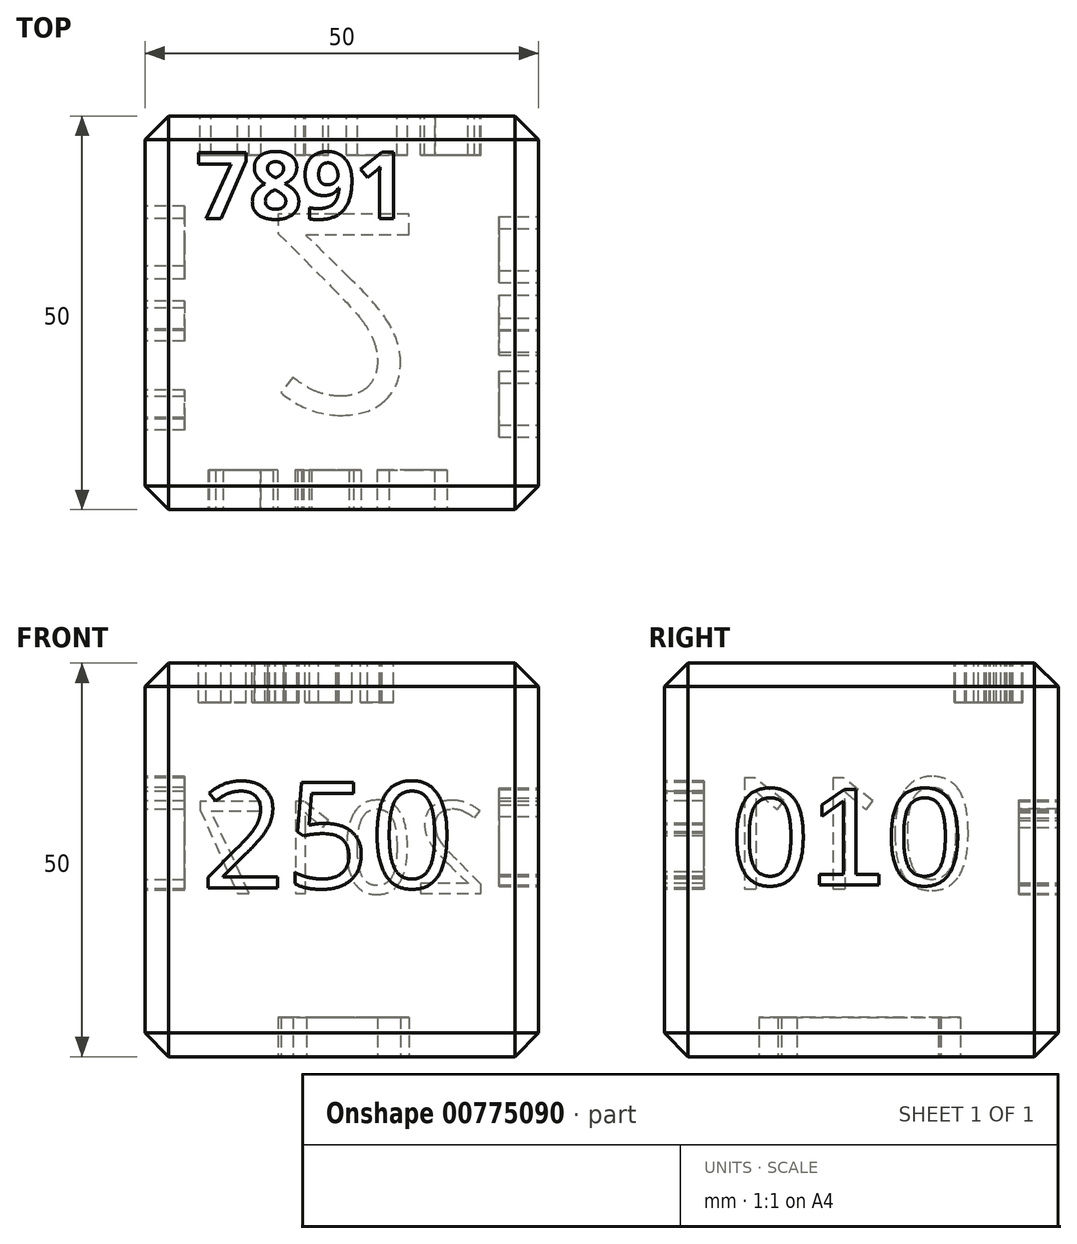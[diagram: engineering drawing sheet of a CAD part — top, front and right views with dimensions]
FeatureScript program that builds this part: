
annotation { "Feature Type Name" : "Feature", "Feature Type Description" : "" }
export const myFeature = defineFeature(function(context is Context, id is Id, definition is map)
    precondition{}
    {
        {
            var Q0;
            Q0=qCreatedBy(makeId("Top.planeOp"),FACE);
            var sketch = newSketch(context, id + "F0", { "sketchPlane" : qUnion([Q0])});
            skLineSegment(sketch, "E0.bottom", {"start": v(-32.37, 24.04) * mm, "end": v(17.63, 24.04) * mm});
            skLineSegment(sketch, "E0.top", {"start": v(-32.37, -25.96) * mm, "end": v(17.63, -25.96) * mm});
            skLineSegment(sketch, "E0.left", {"start": v(-32.37, 24.04) * mm, "end": v(-32.37, -25.96) * mm});
            skLineSegment(sketch, "E0.right", {"start": v(17.63, 24.04) * mm, "end": v(17.63, -25.96) * mm});
            skSolve(sketch);
        }
        {
            var Q0;
            Q0=makeQuery(id+"F0.imprint","IMPRINT",FACE,{"disambiguationData":[TD([[makeQuery(id+"F0.imprint","IMPRINT",EDGE,{"derivedFrom":sQuery(id+"F0.wireOp",EDGE,"E0.bottom")}),-1.0]])]});
            extrude(context, id + "F1", {"entities" : qUnion([Q0]), "depth" : 50 * mm, "offsetDistance" : 25 * mm});
        }
        {
            var Q0;
            Q0=makeQuery(id+"F1.opExtrude","CAP_EDGE",EDGE,{"disambiguationData":[OSD([sQuery(id+"F0.wireOp",EDGE,"E0.right")])],"isStart":false});
            var Q1;
            Q1=makeQuery(id+"F1.opExtrude","CAP_EDGE",EDGE,{"disambiguationData":[OSD([sQuery(id+"F0.wireOp",EDGE,"E0.top")])],"isStart":false});
            var Q2;
            Q2=makeQuery(id+"F1.opExtrude","CAP_EDGE",EDGE,{"disambiguationData":[OSD([sQuery(id+"F0.wireOp",EDGE,"E0.left")])],"isStart":false});
            var Q3;
            Q3=makeQuery(id+"F1.opExtrude","CAP_EDGE",EDGE,{"disambiguationData":[OSD([sQuery(id+"F0.wireOp",EDGE,"E0.bottom")])],"isStart":false});
            var Q4;
            Q4=makeQuery(id+"F1.opExtrude","CAP_EDGE",EDGE,{"disambiguationData":[OSD([sQuery(id+"F0.wireOp",EDGE,"E0.top")])],"isStart":true});
            var Q5;
            Q5=makeQuery(id+"F1.opExtrude","CAP_EDGE",EDGE,{"disambiguationData":[OSD([sQuery(id+"F0.wireOp",EDGE,"E0.left")])],"isStart":true});
            var Q6;
            Q6=makeQuery(id+"F1.opExtrude","CAP_EDGE",EDGE,{"disambiguationData":[OSD([sQuery(id+"F0.wireOp",EDGE,"E0.bottom")])],"isStart":true});
            var Q7;
            Q7=makeQuery(id+"F1.opExtrude","CAP_EDGE",EDGE,{"disambiguationData":[OSD([sQuery(id+"F0.wireOp",EDGE,"E0.right")])],"isStart":true});
            var Q8;
            Q8=makeQuery(id+"F1.opExtrude","SWEPT_EDGE",EDGE,{"disambiguationData":[OSD([sQuery(id+"F0.wireOp",EDGE,"E0.bottom"),sQuery(id+"F0.wireOp",EDGE,"E0.right")])]});
            var Q9;
            Q9=makeQuery(id+"F1.opExtrude","SWEPT_EDGE",EDGE,{"disambiguationData":[OSD([sQuery(id+"F0.wireOp",EDGE,"E0.bottom"),sQuery(id+"F0.wireOp",EDGE,"E0.left")])]});
            var Q10;
            Q10=makeQuery(id+"F1.opExtrude","SWEPT_EDGE",EDGE,{"disambiguationData":[OSD([sQuery(id+"F0.wireOp",EDGE,"E0.top"),sQuery(id+"F0.wireOp",EDGE,"E0.left")])]});
            var Q11;
            Q11=makeQuery(id+"F1.opExtrude","SWEPT_EDGE",EDGE,{"disambiguationData":[OSD([sQuery(id+"F0.wireOp",EDGE,"E0.top"),sQuery(id+"F0.wireOp",EDGE,"E0.right")])]});
            chamfer(context, id + "F2", {"entities" : qUnion([Q0, Q1, Q2, Q3, Q4, Q5, Q6, Q7, Q8, Q9, Q10, Q11]), "width" : 3 * mm, "tangentPropagation" : true});
        }
        {
            var Q0;
            Q0=makeQuery(id+"F1.opExtrude","CAP_FACE",FACE,{"disambiguationData":[OSD([sQuery(id+"F0.wireOp",EDGE,"E0.bottom"),sQuery(id+"F0.wireOp",EDGE,"E0.top"),sQuery(id+"F0.wireOp",EDGE,"E0.left"),sQuery(id+"F0.wireOp",EDGE,"E0.right")])],"isStart":false});
            var sketch = newSketch(context, id + "F3", { "sketchPlane" : qUnion([Q0])});
            skText(sketch, "E1", { "text": "7891\n", "fontName": "OpenSans-Bold.ttf"});
            const initialGuessF3  = {"E1": [-0.02589, 0.011, 1, 0, 0.0085]};
            skSetInitialGuess(sketch, initialGuessF3);
            skSolve(sketch);
        }
        {
            var Q0;
            Q0 = qSketchRegion(id + "F3", true);
            extrude(context, id + "F4", {"entities" : qUnion([Q0]), "operationType" : NewBodyOperationType.REMOVE, "oppositeDirection" : true, "depth" : 5 * mm, "offsetDistance" : 25 * mm});
        }
        {
            var Q0;
            Q0=makeQuery(id+"F1.opExtrude","CAP_FACE",FACE,{"disambiguationData":[OSD([sQuery(id+"F0.wireOp",EDGE,"E0.bottom"),sQuery(id+"F0.wireOp",EDGE,"E0.top"),sQuery(id+"F0.wireOp",EDGE,"E0.left"),sQuery(id+"F0.wireOp",EDGE,"E0.right")])],"isStart":true});
            var sketch = newSketch(context, id + "F5", { "sketchPlane" : qUnion([Q0])});
            skText(sketch, "E2", { "text": "2", "fontName": "OpenSans-Regular.ttf"});
            const initialGuessF5  = {"E2": [-0.01716, -0.0116, 1, 0, 0.02545]};
            skSetInitialGuess(sketch, initialGuessF5);
            skSolve(sketch);
        }
        {
            var Q0;
            Q0 = qSketchRegion(id + "F5", true);
            extrude(context, id + "F6", {"entities" : qUnion([Q0]), "operationType" : NewBodyOperationType.REMOVE, "oppositeDirection" : true, "depth" : 5 * mm, "offsetDistance" : 25 * mm});
        }
        {
            var Q0;
            Q0=makeQuery(id+"F1.opExtrude","SWEPT_FACE",FACE,{"disambiguationData":[OSD([sQuery(id+"F0.wireOp",EDGE,"E0.bottom")])]});
            var sketch = newSketch(context, id + "F7", { "sketchPlane" : qUnion([Q0])});
            skText(sketch, "E3", { "text": "2017", "fontName": "OpenSans-Regular.ttf"});
            const initialGuessF7  = {"E3": [-0.01111, 0.02076, 1, 0, 0.01175]};
            skSetInitialGuess(sketch, initialGuessF7);
            skSolve(sketch);
        }
        {
            var Q0;
            Q0 = qSketchRegion(id + "F7", true);
            extrude(context, id + "F8", {"entities" : qUnion([Q0]), "operationType" : NewBodyOperationType.REMOVE, "oppositeDirection" : true, "depth" : 5 * mm, "offsetDistance" : 25 * mm});
        }
        {
            var Q0;
            Q0=makeQuery(id+"F1.opExtrude","SWEPT_FACE",FACE,{"disambiguationData":[OSD([sQuery(id+"F0.wireOp",EDGE,"E0.right")])]});
            var sketch = newSketch(context, id + "F9", { "sketchPlane" : qUnion([Q0])});
            skText(sketch, "E4", { "text": "010", "fontName": "Arimo-Regular.ttf"});
            const initialGuessF9  = {"E4": [-0.01746, 0.02182, 1, 0, 0.0127]};
            skSetInitialGuess(sketch, initialGuessF9);
            skSolve(sketch);
        }
        {
            var Q0;
            Q0=makeQuery(id+"F1.opExtrude","SWEPT_FACE",FACE,{"disambiguationData":[OSD([sQuery(id+"F0.wireOp",EDGE,"E0.top")])]});
            var sketch = newSketch(context, id + "F10", { "sketchPlane" : qUnion([Q0])});
            skText(sketch, "E5", { "text": "250", "fontName": "OpenSans-Regular.ttf"});
            const initialGuessF10  = {"E5": [-0.02529, 0.02144, 1, 0, 0.01352]};
            skSetInitialGuess(sketch, initialGuessF10);
            skSolve(sketch);
        }
        {
            var Q0;
            Q0 = qSketchRegion(id + "F9", true);
            extrude(context, id + "F11", {"entities" : qUnion([Q0]), "operationType" : NewBodyOperationType.REMOVE, "oppositeDirection" : true, "depth" : 5 * mm, "offsetDistance" : 25 * mm});
        }
        {
            var Q0;
            Q0 = qSketchRegion(id + "F10", true);
            extrude(context, id + "F12", {"entities" : qUnion([Q0]), "operationType" : NewBodyOperationType.REMOVE, "oppositeDirection" : true, "depth" : 5 * mm, "offsetDistance" : 25 * mm});
        }
        {
            var Q0;
            Q0=makeQuery(id+"F1.opExtrude","SWEPT_FACE",FACE,{"disambiguationData":[OSD([sQuery(id+"F0.wireOp",EDGE,"E0.left")])]});
            var sketch = newSketch(context, id + "F13", { "sketchPlane" : qUnion([Q0])});
            skText(sketch, "E6", { "text": "011", "fontName": "OpenSans-Regular.ttf"});
            const initialGuessF13  = {"E6": [-0.0136, 0.0213, 1, 0, 0.0142]};
            skSetInitialGuess(sketch, initialGuessF13);
            skSolve(sketch);
        }
        {
            var Q0;
            Q0 = qSketchRegion(id + "F13", true);
            extrude(context, id + "F14", {"entities" : qUnion([Q0]), "operationType" : NewBodyOperationType.REMOVE, "oppositeDirection" : true, "depth" : 5 * mm, "offsetDistance" : 25 * mm});
        }
    });
